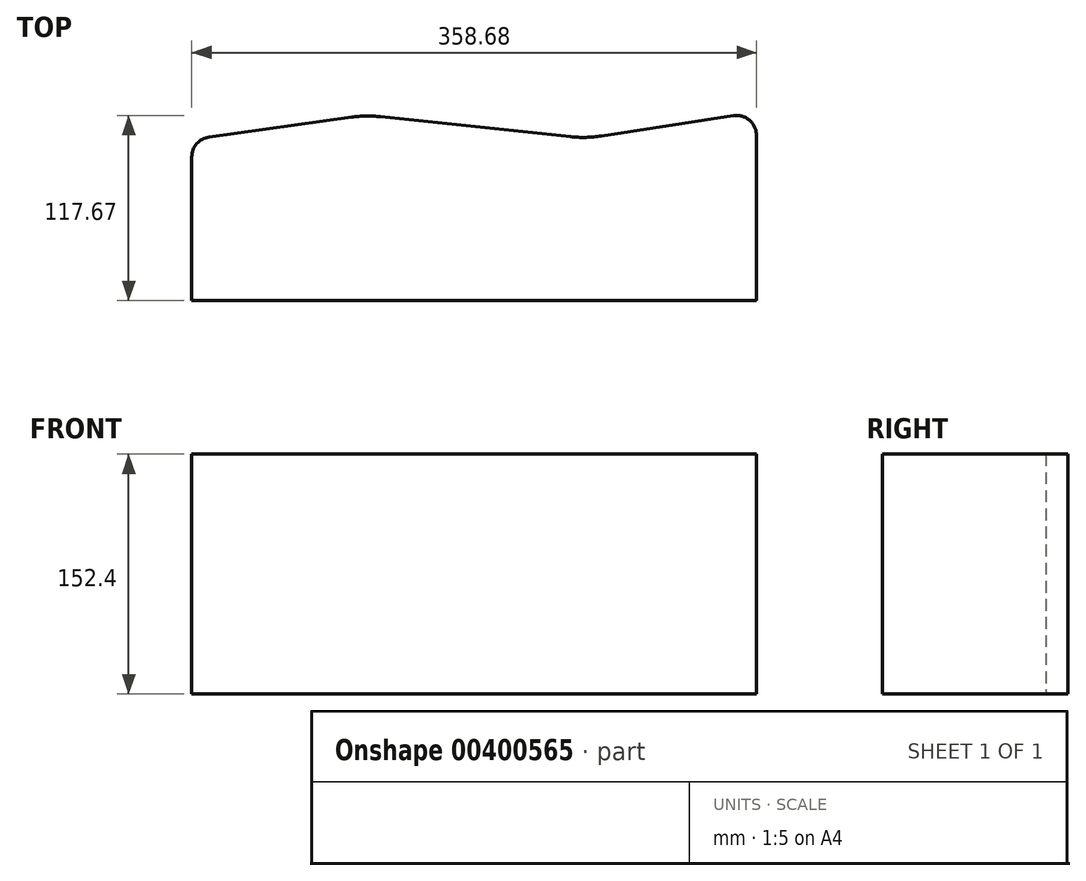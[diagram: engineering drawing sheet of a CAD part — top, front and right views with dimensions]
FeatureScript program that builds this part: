
annotation { "Feature Type Name" : "Feature", "Feature Type Description" : "" }
export const myFeature = defineFeature(function(context is Context, id is Id, definition is map)
    precondition{}
    {
        {
            var Q0;
            Q0=qCreatedBy(makeId("Top.planeOp"),FACE);
            var sketch = newSketch(context, id + "F0", { "sketchPlane" : qUnion([Q0])});
            skLineSegment(sketch, "E0", {"start": v(-179.34, 0) * mm, "end": v(179.34, 0) * mm});
            skLineSegment(sketch, "E1", {"start": v(-179.34, 0) * mm, "end": v(-179.34, 91.31) * mm});
            skLineSegment(sketch, "E2", {"start": v(-168.4, 103.9) * mm, "end": v(-77.9, 116.55) * mm});
            skLineSegment(sketch, "E3", {"start": v(-59.34, 116.86) * mm, "end": v(61.21, 104.12) * mm});
            skLineSegment(sketch, "E4", {"start": v(80.84, 104.59) * mm, "end": v(164.7, 117.52) * mm});
            skLineSegment(sketch, "E5", {"start": v(179.34, 104.97) * mm, "end": v(179.34, 0) * mm});
            skPoint(sketch, "E6.visualSharp", {"position": v(-179.34, 102.36) * mm});
            skArc(sketch, "E6.filletArc", {"start": v(-168.4, 103.9) * mm, "mid": v(-176.22, 99.65) * mm, "end": v(-179.34, 91.31) * mm});
            skPoint(sketch, "E7.visualSharp", {"position": v(179.34, 119.77) * mm});
            skArc(sketch, "E7.filletArc", {"start": v(179.34, 104.97) * mm, "mid": v(174.9, 114.6) * mm, "end": v(164.7, 117.52) * mm});
            skPoint(sketch, "E8.visualSharp", {"position": v(-68.64, 117.85) * mm});
            skArc(sketch, "E8.filletArc", {"start": v(-59.34, 116.86) * mm, "mid": v(-68.63, 117.28) * mm, "end": v(-77.9, 116.55) * mm});
            skPoint(sketch, "E9.visualSharp", {"position": v(71.06, 103.08) * mm});
            skArc(sketch, "E9.filletArc", {"start": v(61.21, 104.12) * mm, "mid": v(71.04, 103.72) * mm, "end": v(80.84, 104.59) * mm});
            skSolve(sketch);
        }
        {
            var Q0;
            Q0 = qSketchRegion(id + "F0", true);
            extrude(context, id + "F1", {"entities" : qUnion([Q0]), "depth" : 152.4 * mm});
        }
    });
